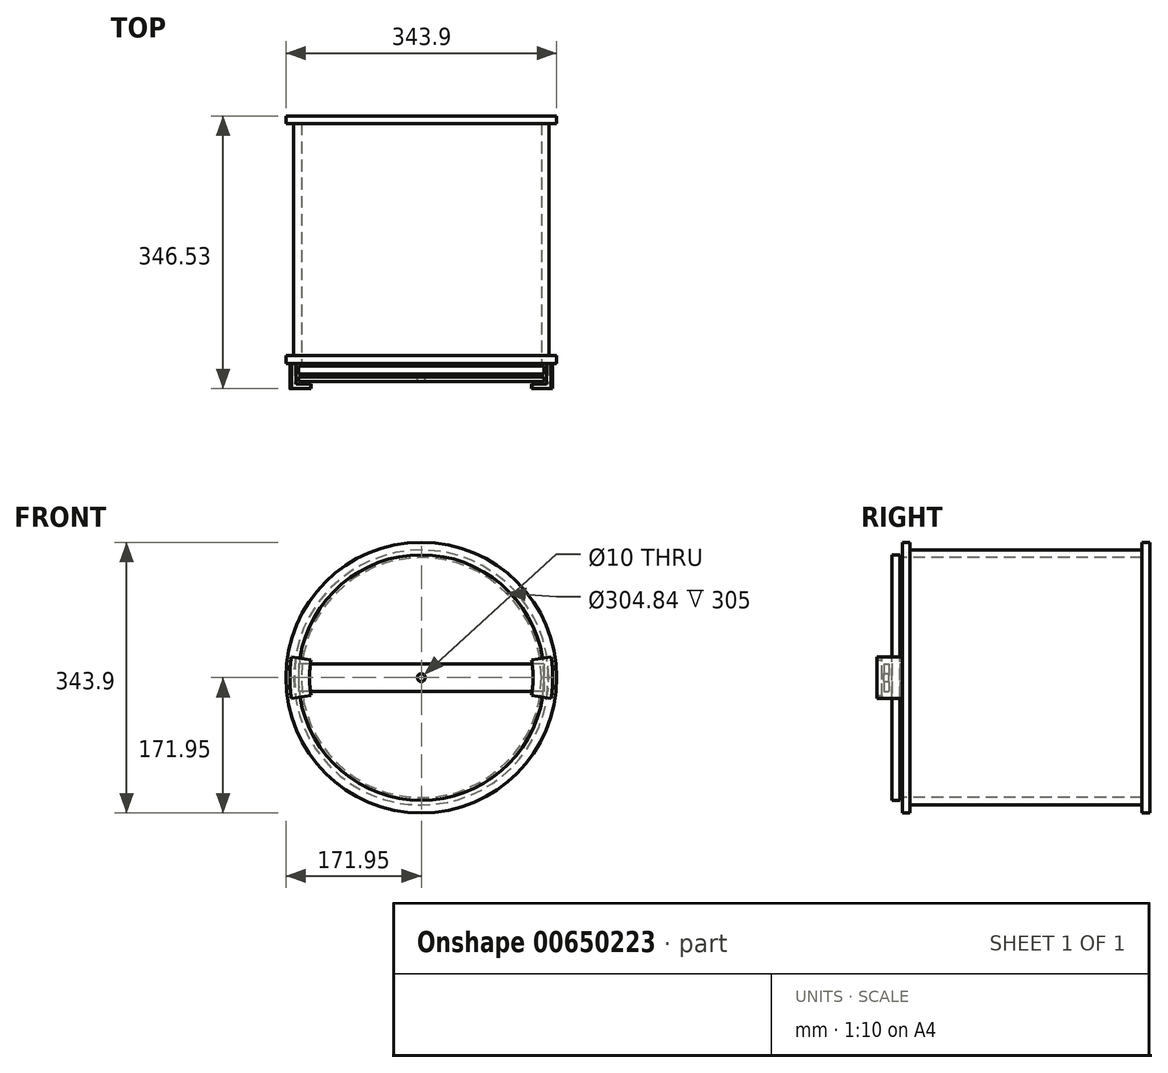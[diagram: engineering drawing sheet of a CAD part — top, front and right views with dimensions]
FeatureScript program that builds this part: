
annotation { "Feature Type Name" : "Feature", "Feature Type Description" : "" }
export const myFeature = defineFeature(function(context is Context, id is Id, definition is map)
    precondition{}
    {
        {
            var Q0;
            Q0=qCreatedBy(makeId("Front.planeOp"),FACE);
            var sketch = newSketch(context, id + "F0", { "sketchPlane" : qUnion([Q0])});
            skCircle(sketch, "E0", {"center": v(0, 0) * mm, "radius": 161.95 * mm});
            skSolve(sketch);
        }
        {
            var Q0;
            Q0 = qSketchRegion(id + "F0", true);
            extrude(context, id + "F1", {"entities" : qUnion([Q0]), "oppositeDirection" : true, "depth" : 314.53 * mm, "offsetDistance" : 25 * mm});
        }
        {
            var Q0;
            Q0=makeQuery(id+"F1.opExtrude","CAP_FACE",FACE,{"disambiguationData":[OSD([sQuery(id+"F0.wireOp",EDGE,"E0")])],"isStart":true});
            shell(context, id + "F2", {"entities" : qUnion([Q0]), "thickness" : 9.53 * mm});
        }
        {
            var Q0;
            Q0=makeQuery(id+"F1.opExtrude","CAP_FACE",FACE,{"disambiguationData":[OSD([sQuery(id+"F0.wireOp",EDGE,"E0")])],"isStart":true});
            var sketch = newSketch(context, id + "F3", { "sketchPlane" : qUnion([Q0])});
            skArc(sketch, "E1", {"start": v(155.96, -25) * mm, "mid": v(157.95, 0) * mm, "end": v(155.96, 25) * mm});
            skPoint(sketch, "E1.endSnap0", {"position": v(157.95, 0) * mm});
            skLineSegment(sketch, "E2", {"start": v(0, 0) * mm, "end": v(265.94, 0) * mm, "construction": true});
            skSolve(sketch);
        }
        {
            var Q0;
            Q0=qCreatedBy(makeId("Top.planeOp"),FACE);
            var sketch = newSketch(context, id + "F4", { "sketchPlane" : qUnion([Q0])});
            skLineSegment(sketch, "E3", {"start": v(166.95, 0) * mm, "end": v(166.95, -32) * mm});
            skLineSegment(sketch, "E4", {"start": v(166.95, -32) * mm, "end": v(141.95, -32) * mm});
            skLineSegment(sketch, "E5", {"start": v(141.95, -32) * mm, "end": v(141.95, -26) * mm});
            skLineSegment(sketch, "E6", {"start": v(141.95, -26) * mm, "end": v(160.95, -26) * mm});
            skLineSegment(sketch, "E7", {"start": v(160.95, -26) * mm, "end": v(160.95, 0) * mm});
            skLineSegment(sketch, "E8", {"start": v(160.95, 0) * mm, "end": v(166.95, 0) * mm});
            skLineSegment(sketch, "E9.MirrorCS", {"start": v(-160.95, -26) * mm, "end": v(-160.95, 0) * mm});
            skLineSegment(sketch, "E10.MirrorCS", {"start": v(-141.95, -26) * mm, "end": v(-160.95, -26) * mm});
            skLineSegment(sketch, "E11.MirrorCS", {"start": v(-141.95, -32) * mm, "end": v(-141.95, -26) * mm});
            skLineSegment(sketch, "E12.MirrorCS", {"start": v(-166.95, -32) * mm, "end": v(-141.95, -32) * mm});
            skLineSegment(sketch, "E13.MirrorCS", {"start": v(-166.95, 0) * mm, "end": v(-166.95, -32) * mm});
            skLineSegment(sketch, "E14.MirrorCS", {"start": v(-160.95, 0) * mm, "end": v(-166.95, 0) * mm});
            skSolve(sketch);
        }
        {
            var Q0;
            Q0=makeQuery(id+"F4.imprint","IMPRINT",FACE,{"disambiguationData":[TD([[makeQuery(id+"F4.imprint","IMPRINT",EDGE,{"derivedFrom":sQuery(id+"F4.wireOp",EDGE,"E3")}),-1.0]])]});
            var Q1;
            Q1=makeQuery(id+"F4.imprint","IMPRINT",FACE,{"disambiguationData":[TD([[makeQuery(id+"F4.imprint","IMPRINT",EDGE,{"derivedFrom":sQuery(id+"F4.wireOp",EDGE,"E9.MirrorCS")}),1.0]])]});
            var Q2;
            Q2=sQuery(id+"F3.wireOp",EDGE,"E1");
            sweep(context, id + "F5", {"operationType" : NewBodyOperationType.ADD, "profiles" : qUnion([Q0, Q1]), "path" : qUnion([Q2])});
        }
        {
            var Q0;
            Q0=qCreatedBy(makeId("Right.planeOp"),FACE);
            var sketch = newSketch(context, id + "F6", { "sketchPlane" : qUnion([Q0])});
            skLineSegment(sketch, "E15.bottom", {"start": v(0, 161.95) * mm, "end": v(10, 161.95) * mm});
            skLineSegment(sketch, "E15.top", {"start": v(0, 171.95) * mm, "end": v(10, 171.95) * mm});
            skLineSegment(sketch, "E15.left", {"start": v(0, 161.95) * mm, "end": v(0, 171.95) * mm});
            skLineSegment(sketch, "E15.right", {"start": v(10, 161.95) * mm, "end": v(10, 171.95) * mm});
            skLineSegment(sketch, "E16", {"start": v(0, 0) * mm, "end": v(314.53, 0) * mm, "construction": true});
            skLineSegment(sketch, "E17", {"start": v(157.26, 0) * mm, "end": v(157.26, 214.8) * mm, "construction": true});
            skLineSegment(sketch, "E18.MirrorCS", {"start": v(314.53, 161.95) * mm, "end": v(314.53, 171.95) * mm});
            skLineSegment(sketch, "E19.MirrorCS", {"start": v(314.53, 171.95) * mm, "end": v(304.53, 171.95) * mm});
            skLineSegment(sketch, "E20.MirrorCS", {"start": v(304.53, 161.95) * mm, "end": v(304.53, 171.95) * mm});
            skLineSegment(sketch, "E21.MirrorCS", {"start": v(314.53, 161.95) * mm, "end": v(304.53, 161.95) * mm});
            skSolve(sketch);
        }
        {
            var Q0;
            Q0=makeQuery(id+"F6.imprint","IMPRINT",FACE,{"disambiguationData":[TD([[makeQuery(id+"F6.imprint","IMPRINT",EDGE,{"derivedFrom":sQuery(id+"F6.wireOp",EDGE,"E15.bottom")}),1.0]])]});
            var Q1;
            Q1=makeQuery(id+"F6.imprint","IMPRINT",FACE,{"disambiguationData":[TD([[makeQuery(id+"F6.imprint","IMPRINT",EDGE,{"derivedFrom":sQuery(id+"F6.wireOp",EDGE,"E18.MirrorCS")}),1.0]])]});
            var Q2;
            {var subQ0=sQuery(id+"F0.wireOp",EDGE,"E0");Q2=makeQuery(id+"F2.opShell","OFFSET_EDGE",EDGE,{"disambiguationData":[OSD([subQ0]),TDD([makeQuery(id+"F1.opExtrude","CAP_EDGE",EDGE,{"disambiguationData":[OSD([subQ0])],"isStart":true})])]});}
            revolve(context, id + "F7", {"operationType" : NewBodyOperationType.ADD, "entities" : qUnion([Q0, Q1]), "axis" : qUnion([Q2]), "revolveType" : RevolveType.FULL});
        }
        {
            var Q0;
            Q0=qCreatedBy(makeId("Front.planeOp"),FACE);
            cPlane(context, id + "F8", {"entities" : qUnion([Q0]), "cplaneType" : CPlaneType.OFFSET, "offset" : 3 * mm, "width" : 150 * mm, "height" : 150 * mm});
        }
        {
            var Q0;
            Q0=qCreatedBy(id+"F8.planeOp",FACE);
            var sketch = newSketch(context, id + "F9", { "sketchPlane" : qUnion([Q0])});
            skCircle(sketch, "E22", {"center": v(0, 0) * mm, "radius": 156 * mm});
            skSolve(sketch);
        }
        {
            var Q0;
            Q0 = qSketchRegion(id + "F9", true);
            extrude(context, id + "F10", {"entities" : qUnion([Q0]), "depth" : 10 * mm, "offsetDistance" : 25 * mm});
        }
        {
            var Q0;
            Q0=qCreatedBy(makeId("Front.planeOp"),FACE);
            cPlane(context, id + "F11", {"entities" : qUnion([Q0]), "cplaneType" : CPlaneType.OFFSET, "offset" : 17 * mm, "width" : 150 * mm, "height" : 150 * mm});
        }
        {
            var Q0;
            Q0=qCreatedBy(id+"F11.planeOp",FACE);
            var sketch = newSketch(context, id + "F12", { "sketchPlane" : qUnion([Q0])});
            skLineSegment(sketch, "E23.bottom", {"start": v(156, 17.5) * mm, "end": v(-156, 17.5) * mm});
            skLineSegment(sketch, "E23.top", {"start": v(156, -17.5) * mm, "end": v(-156, -17.5) * mm});
            skLineSegment(sketch, "E23.left", {"start": v(156, 17.5) * mm, "end": v(156, -17.5) * mm});
            skLineSegment(sketch, "E23.right", {"start": v(-156, 17.5) * mm, "end": v(-156, -17.5) * mm});
            skPoint(sketch, "E23.middle", {"position": v(0, 0) * mm});
            skCircle(sketch, "E24", {"center": v(0, 0) * mm, "radius": 5 * mm});
            skSolve(sketch);
        }
        {
            var Q0;
            Q0=makeQuery(id+"F12.imprint","IMPRINT",FACE,{"disambiguationData":[TD([[makeQuery(id+"F12.imprint","IMPRINT",EDGE,{"derivedFrom":sQuery(id+"F12.wireOp",EDGE,"E23.bottom")}),1.0]])]});
            extrude(context, id + "F13", {"entities" : qUnion([Q0]), "depth" : 6 * mm, "offsetDistance" : 25 * mm});
        }
    });
